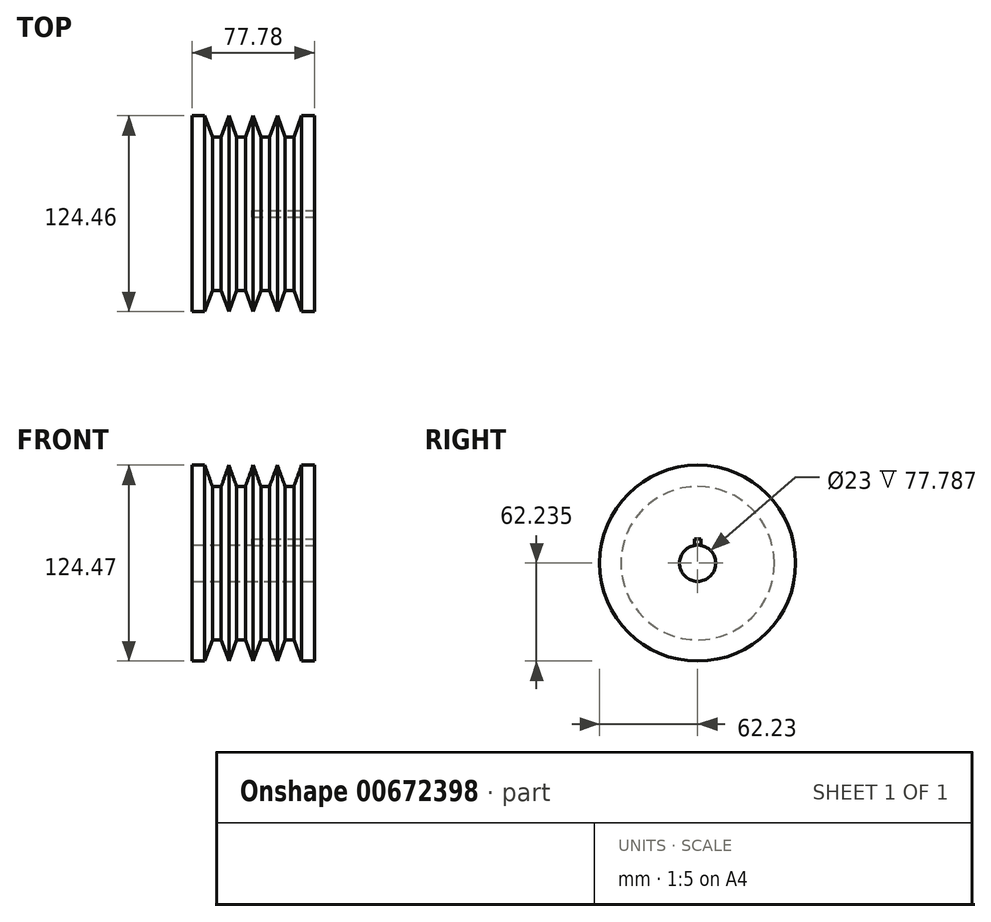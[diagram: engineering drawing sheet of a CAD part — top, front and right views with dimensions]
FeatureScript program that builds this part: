
annotation { "Feature Type Name" : "Feature", "Feature Type Description" : "" }
export const myFeature = defineFeature(function(context is Context, id is Id, definition is map)
    precondition{}
    {
        {
            var Q0;
            Q0=qCreatedBy(makeId("Front.planeOp"),FACE);
            var sketch = newSketch(context, id + "F0", { "sketchPlane" : qUnion([Q0])});
            skLineSegment(sketch, "E0.bottom", {"start": v(-38.9, 31.12) * mm, "end": v(-30.76, 31.12) * mm});
            skLineSegment(sketch, "E0.top", {"start": v(-38.9, -31.11) * mm, "end": v(38.9, -31.11) * mm});
            skLineSegment(sketch, "E0.left", {"start": v(-38.9, 31.12) * mm, "end": v(-38.9, -31.11) * mm});
            skLineSegment(sketch, "E0.right", {"start": v(38.9, 31.12) * mm, "end": v(38.9, -31.11) * mm});
            skPoint(sketch, "E0.middle", {"position": v(0, 0) * mm});
            skLineSegment(sketch, "E1.top", {"start": v(-30.76, -31.12) * mm, "end": v(30.76, -31.12) * mm});
            skLineSegment(sketch, "E2", {"start": v(-25.85, 17.62) * mm, "end": v(-20.3, 17.62) * mm});
            skLineSegment(sketch, "E3.direction1", {"start": v(-25.85, 17.62) * mm, "end": v(-20.3, 17.62) * mm, "construction": true});
            skLineSegment(sketch, "E4", {"start": v(-30.76, 31.12) * mm, "end": v(-25.85, 17.62) * mm});
            skLineSegment(sketch, "E5", {"start": v(-20.3, 17.62) * mm, "end": v(-15.38, 31.12) * mm});
            skLineSegment(sketch, "E6.1.0.0", {"start": v(-15.38, 31.12) * mm, "end": v(-10.47, 17.62) * mm});
            skLineSegment(sketch, "E6.1.0.1", {"start": v(-10.47, 17.62) * mm, "end": v(-4.91, 17.62) * mm, "construction": true});
            skLineSegment(sketch, "E6.1.0.2", {"start": v(-4.91, 17.62) * mm, "end": v(0, 31.12) * mm});
            skLineSegment(sketch, "E6.2.0.0", {"start": v(0, 31.12) * mm, "end": v(4.91, 17.62) * mm});
            skLineSegment(sketch, "E6.2.0.1", {"start": v(4.91, 17.62) * mm, "end": v(10.47, 17.62) * mm, "construction": true});
            skLineSegment(sketch, "E6.2.0.2", {"start": v(10.47, 17.62) * mm, "end": v(15.38, 31.12) * mm});
            skLineSegment(sketch, "E6.3.0.0", {"start": v(15.38, 31.12) * mm, "end": v(20.3, 17.62) * mm});
            skLineSegment(sketch, "E6.3.0.1", {"start": v(20.3, 17.62) * mm, "end": v(25.85, 17.62) * mm, "construction": true});
            skLineSegment(sketch, "E6.3.0.2", {"start": v(25.85, 17.62) * mm, "end": v(30.76, 31.12) * mm});
            skLineSegment(sketch, "E6.direction1", {"start": v(-25.85, 17.62) * mm, "end": v(-10.47, 17.62) * mm, "construction": true});
            skLineSegment(sketch, "E7", {"start": v(-10.47, 17.62) * mm, "end": v(-4.91, 17.62) * mm});
            skLineSegment(sketch, "E8", {"start": v(4.91, 17.62) * mm, "end": v(10.47, 17.62) * mm});
            skLineSegment(sketch, "E9", {"start": v(20.3, 17.62) * mm, "end": v(25.85, 17.62) * mm});
            skLineSegment(sketch, "E10.trimOffspring", {"start": v(30.76, 31.12) * mm, "end": v(38.9, 31.12) * mm});
            skSolve(sketch);
        }
        {
            var Q0;
            Q0 = qSketchRegion(id + "F0", true);
            var Q1;
            Q1=sQuery(id+"F0.wireOp",EDGE,"E1.top");
            revolve(context, id + "F1", {"entities" : qUnion([Q0]), "axis" : qUnion([Q1]), "revolveType" : RevolveType.FULL});
        }
        {
            var Q0;
            Q0=makeQuery(id+"F1.opRevolve","SWEPT_FACE",FACE,{"disambiguationData":[OSD([sQuery(id+"F0.wireOp",EDGE,"E0.right")])]});
            var sketch = newSketch(context, id + "F2", { "sketchPlane" : qUnion([Q0])});
            skCircle(sketch, "E11", {"center": v(0, -31.12) * mm, "radius": 11.5 * mm});
            skSolve(sketch);
        }
        {
            var Q0;
            Q0 = qSketchRegion(id + "F2", true);
            extrude(context, id + "F3", {"entities" : qUnion([Q0]), "operationType" : NewBodyOperationType.REMOVE, "oppositeDirection" : true, "depth" : 80.52 * mm, "offsetDistance" : 25.4 * mm});
        }
        {
            var Q0;
            Q0=makeQuery(id+"F1.opRevolve","SWEPT_FACE",FACE,{"disambiguationData":[OSD([sQuery(id+"F0.wireOp",EDGE,"E0.right")])]});
            var sketch = newSketch(context, id + "F4", { "sketchPlane" : qUnion([Q0])});
            skLineSegment(sketch, "E12", {"start": v(0, -15.62) * mm, "end": v(-2, -15.62) * mm});
            skLineSegment(sketch, "E13", {"start": v(-2, -15.62) * mm, "end": v(-2, -19.8) * mm});
            skLineSegment(sketch, "E14", {"start": v(2, -19.8) * mm, "end": v(2, -15.62) * mm});
            skLineSegment(sketch, "E15", {"start": v(2, -15.62) * mm, "end": v(0, -15.62) * mm});
            skSolve(sketch);
        }
        {
            var Q0;
            Q0=makeQuery(id+"F4.imprint","IMPRINT",FACE,{"disambiguationData":[TD([[makeQuery(id+"F4.imprint","IMPRINT",EDGE,{"derivedFrom":sQuery(id+"F4.wireOp",EDGE,"E12")}),1.0]])]});
            extrude(context, id + "F5", {"entities" : qUnion([Q0]), "operationType" : NewBodyOperationType.REMOVE, "oppositeDirection" : true, "depth" : 40 * mm, "offsetDistance" : 25.4 * mm});
        }
    });
